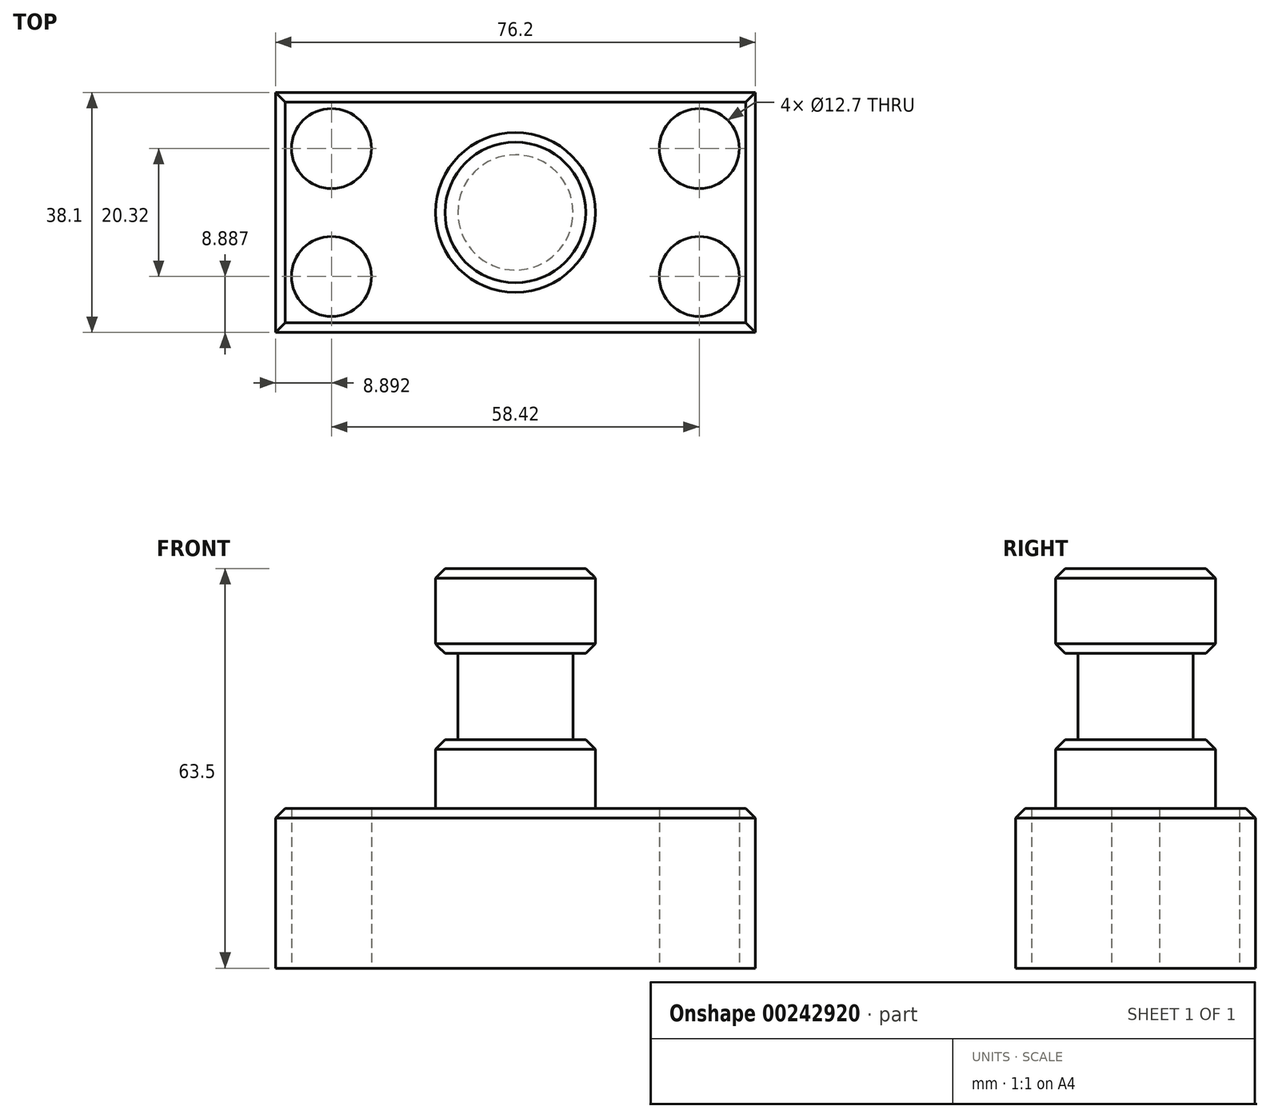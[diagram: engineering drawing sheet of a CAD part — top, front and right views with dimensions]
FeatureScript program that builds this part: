
annotation { "Feature Type Name" : "Feature", "Feature Type Description" : "" }
export const myFeature = defineFeature(function(context is Context, id is Id, definition is map)
    precondition{}
    {
        {
            var Q0;
            Q0=qCreatedBy(makeId("Top.planeOp"),FACE);
            var sketch = newSketch(context, id + "F0", { "sketchPlane" : qUnion([Q0])});
            skLineSegment(sketch, "E0.bottom", {"start": v(-35.27, -6.93) * mm, "end": v(40.93, -6.93) * mm});
            skLineSegment(sketch, "E0.top", {"start": v(-35.27, -45.03) * mm, "end": v(40.93, -45.03) * mm});
            skLineSegment(sketch, "E0.left", {"start": v(-35.27, -6.93) * mm, "end": v(-35.27, -45.03) * mm});
            skLineSegment(sketch, "E0.right", {"start": v(40.93, -6.93) * mm, "end": v(40.93, -45.03) * mm});
            skSolve(sketch);
        }
        {
            var Q0;
            Q0 = qSketchRegion(id + "F0", true);
            extrude(context, id + "F1", {"entities" : qUnion([Q0]), "depth" : 25.4 * mm});
        }
        {
            var Q0;
            Q0=qCreatedBy(makeId("Top.planeOp"),FACE);
            var sketch = newSketch(context, id + "F2", { "sketchPlane" : qUnion([Q0])});
            skCircle(sketch, "E1", {"center": v(-26.38, -15.82) * mm, "radius": 6.35 * mm});
            skCircle(sketch, "E2", {"center": v(-26.38, -36.14) * mm, "radius": 6.35 * mm});
            skCircle(sketch, "E3", {"center": v(32.04, -15.82) * mm, "radius": 6.35 * mm});
            skCircle(sketch, "E4", {"center": v(32.04, -36.14) * mm, "radius": 6.35 * mm});
            skSolve(sketch);
        }
        {
            var Q0;
            Q0=makeQuery(id+"F2.imprint","IMPRINT",FACE,{"disambiguationData":[TD([[makeQuery(id+"F2.imprint","IMPRINT",EDGE,{"derivedFrom":sQuery(id+"F2.wireOp",EDGE,"E1")}),1.0]])]});
            extrude(context, id + "F3", {"entities" : qUnion([Q0]), "operationType" : NewBodyOperationType.REMOVE, "depth" : 25.4 * mm});
        }
        {
            var Q0;
            Q0 = qSketchRegion(id + "F2", true);
            extrude(context, id + "F4", {"entities" : qUnion([Q0]), "operationType" : NewBodyOperationType.REMOVE, "depth" : 25.4 * mm});
        }
        {
            var Q0;
            Q0=makeQuery(id+"F1.opExtrude","CAP_FACE",FACE,{"disambiguationData":[OSD([sQuery(id+"F0.wireOp",EDGE,"E0.bottom"),sQuery(id+"F0.wireOp",EDGE,"E0.top"),sQuery(id+"F0.wireOp",EDGE,"E0.left"),sQuery(id+"F0.wireOp",EDGE,"E0.right")])],"isStart":false});
            var sketch = newSketch(context, id + "F5", { "sketchPlane" : qUnion([Q0])});
            skCircle(sketch, "E5", {"center": v(2.83, -25.98) * mm, "radius": 12.7 * mm});
            skSolve(sketch);
        }
        {
            var Q0;
            Q0 = qSketchRegion(id + "F5", true);
            extrude(context, id + "F6", {"entities" : qUnion([Q0]), "operationType" : NewBodyOperationType.ADD, "depth" : 38.1 * mm});
        }
        {
            var Q0;
            Q0=qCreatedBy(makeId("Right.planeOp"),FACE);
            var sketch = newSketch(context, id + "F7", { "sketchPlane" : qUnion([Q0])});
            skLineSegment(sketch, "E6.bottom", {"start": v(-51.3, 49.99) * mm, "end": v(-34.69, 49.99) * mm});
            skLineSegment(sketch, "E6.top", {"start": v(-51.3, 36.29) * mm, "end": v(-34.69, 36.29) * mm});
            skLineSegment(sketch, "E6.left", {"start": v(-51.3, 49.99) * mm, "end": v(-51.3, 36.29) * mm});
            skLineSegment(sketch, "E6.right", {"start": v(-34.69, 49.99) * mm, "end": v(-34.69, 36.29) * mm});
            skSolve(sketch);
        }
        {
            var Q0;
            Q0 = qSketchRegion(id + "F7", true);
            var Q1;
            Q1=makeQuery(id+"F6.opExtrude","CAP_EDGE",EDGE,{"disambiguationData":[OSD([sQuery(id+"F5.wireOp",EDGE,"E5")])],"isStart":false});
            revolve(context, id + "F8", {"operationType" : NewBodyOperationType.REMOVE, "entities" : qUnion([Q0]), "axis" : qUnion([Q1]), "revolveType" : RevolveType.FULL, "oppositeDirection" : true});
        }
        {
            var Q0;
            Q0=makeQuery(id+"F1.opExtrude","CAP_EDGE",EDGE,{"disambiguationData":[OSD([sQuery(id+"F0.wireOp",EDGE,"E0.right")])],"isStart":false});
            chamfer(context, id + "F9", {"entities" : qUnion([Q0]), "width" : 1.52 * mm, "tangentPropagation" : true});
        }
        {
            var Q0;
            Q0=makeQuery(id+"F1.opExtrude","CAP_EDGE",EDGE,{"disambiguationData":[OSD([sQuery(id+"F0.wireOp",EDGE,"E0.bottom")])],"isStart":false});
            var Q1;
            Q1=makeQuery(id+"F1.opExtrude","CAP_EDGE",EDGE,{"disambiguationData":[OSD([sQuery(id+"F0.wireOp",EDGE,"E0.left")])],"isStart":false});
            chamfer(context, id + "F10", {"entities" : qUnion([Q0, Q1]), "width" : 1.52 * mm, "tangentPropagation" : true});
        }
        {
            var Q0;
            Q0=makeQuery(id+"F1.opExtrude","CAP_EDGE",EDGE,{"disambiguationData":[OSD([sQuery(id+"F0.wireOp",EDGE,"E0.top")])],"isStart":false});
            var Q1;
            Q1=makeQuery(id+"F8.boolean.opBoolean","INTERSECT",EDGE,{"derivedFrom":[makeQuery(id+"F6.opExtrude","SWEPT_FACE",FACE,{"disambiguationData":[OSD([sQuery(id+"F5.wireOp",EDGE,"E5")])]}),makeQuery(id+"F8.opRevolve","SWEPT_FACE",FACE,{"disambiguationData":[OSD([sQuery(id+"F7.wireOp",EDGE,"E6.top")])]})]});
            var Q2;
            Q2=makeQuery(id+"F8.boolean.opBoolean","INTERSECT",EDGE,{"derivedFrom":[makeQuery(id+"F6.opExtrude","SWEPT_FACE",FACE,{"disambiguationData":[OSD([sQuery(id+"F5.wireOp",EDGE,"E5")])]}),makeQuery(id+"F8.opRevolve","SWEPT_FACE",FACE,{"disambiguationData":[OSD([sQuery(id+"F7.wireOp",EDGE,"E6.bottom")])]})]});
            var Q3;
            Q3=makeQuery(id+"F6.opExtrude","CAP_EDGE",EDGE,{"disambiguationData":[OSD([sQuery(id+"F5.wireOp",EDGE,"E5")])],"isStart":false});
            chamfer(context, id + "F11", {"entities" : qUnion([Q0, Q1, Q2, Q3]), "width" : 1.52 * mm, "tangentPropagation" : true});
        }
    });
